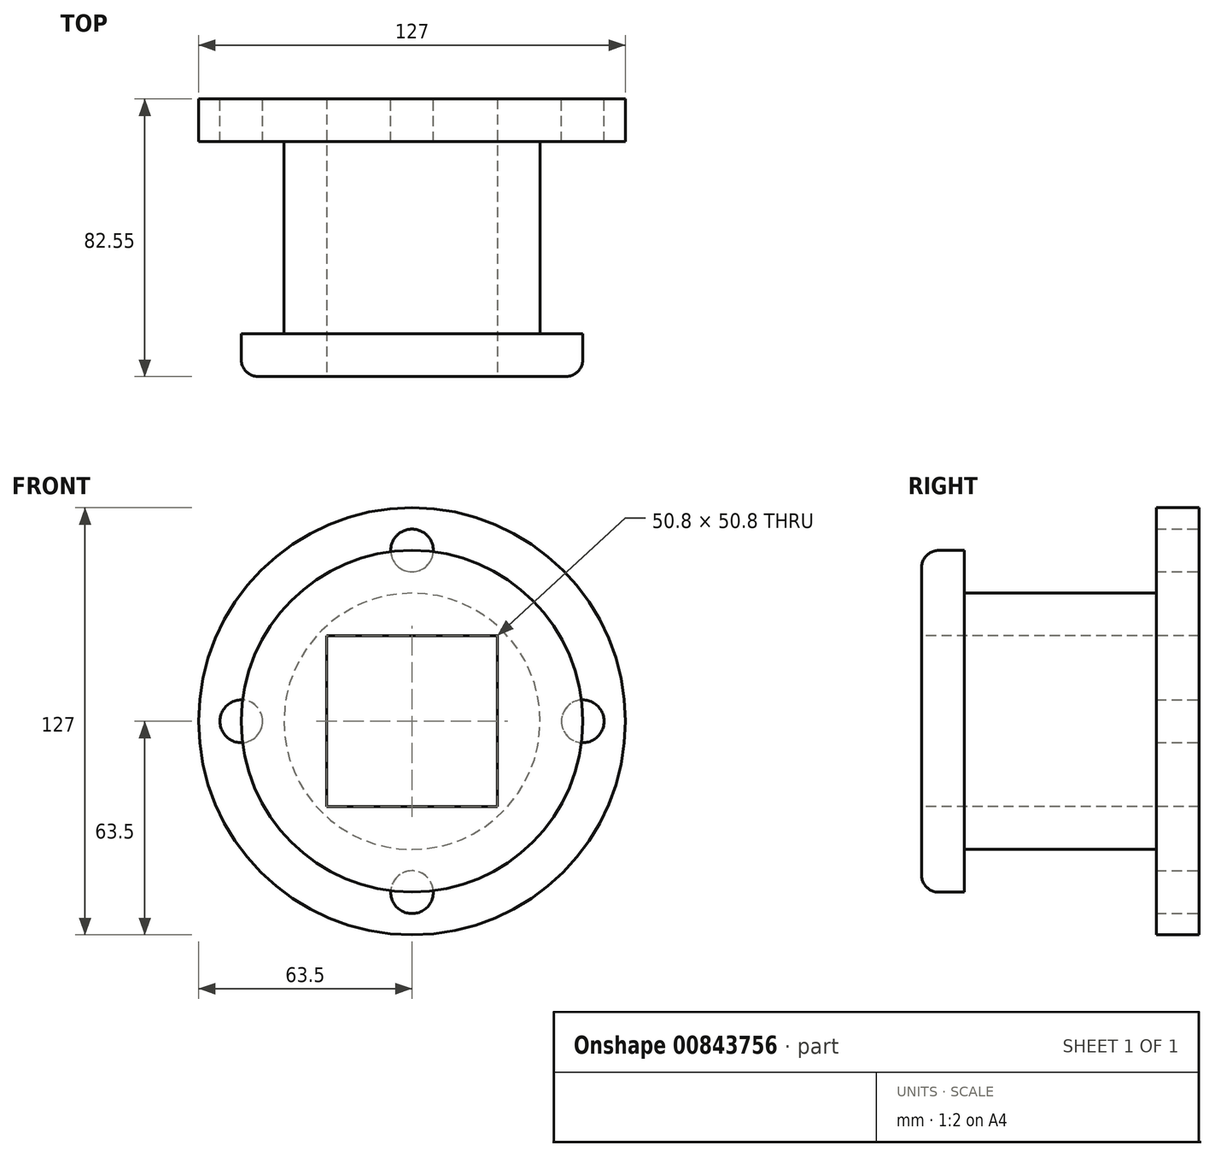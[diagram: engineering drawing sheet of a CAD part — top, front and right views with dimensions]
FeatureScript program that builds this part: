
annotation { "Feature Type Name" : "Feature", "Feature Type Description" : "" }
export const myFeature = defineFeature(function(context is Context, id is Id, definition is map)
    precondition{}
    {
        {
            var Q0;
            Q0=qCreatedBy(makeId("Front.planeOp"),FACE);
            var sketch = newSketch(context, id + "F0", { "sketchPlane" : qUnion([Q0])});
            skCircle(sketch, "E0", {"center": v(0, 0) * mm, "radius": 63.5 * mm});
            skSolve(sketch);
        }
        {
            var Q0;
            Q0 = qSketchRegion(id + "F0", true);
            extrude(context, id + "F1", {"entities" : qUnion([Q0]), "depth" : 12.7 * mm, "offsetDistance" : 25.4 * mm});
        }
        {
            var Q0;
            Q0=makeQuery(id+"F1.opExtrude","CAP_FACE",FACE,{"disambiguationData":[OSD([sQuery(id+"F0.wireOp",EDGE,"E0")])],"isStart":false});
            var sketch = newSketch(context, id + "F2", { "sketchPlane" : qUnion([Q0])});
            skCircle(sketch, "E1", {"center": v(0, 0) * mm, "radius": 38.1 * mm});
            skSolve(sketch);
        }
        {
            var Q0;
            Q0 = qSketchRegion(id + "F2", true);
            extrude(context, id + "F3", {"entities" : qUnion([Q0]), "operationType" : NewBodyOperationType.ADD, "depth" : 57.15 * mm, "offsetDistance" : 25.4 * mm});
        }
        {
            var Q0;
            Q0=makeQuery(id+"F3.opExtrude","CAP_FACE",FACE,{"disambiguationData":[OSD([sQuery(id+"F2.wireOp",EDGE,"E1")])],"isStart":false});
            var sketch = newSketch(context, id + "F4", { "sketchPlane" : qUnion([Q0])});
            skCircle(sketch, "E2", {"center": v(0, 0) * mm, "radius": 50.8 * mm});
            skSolve(sketch);
        }
        {
            var Q0;
            Q0 = qSketchRegion(id + "F4", true);
            extrude(context, id + "F5", {"entities" : qUnion([Q0]), "operationType" : NewBodyOperationType.ADD, "depth" : 12.7 * mm, "offsetDistance" : 25.4 * mm});
        }
        {
            var Q0;
            Q0=makeQuery(id+"F5.opExtrude","CAP_FACE",FACE,{"disambiguationData":[OSD([sQuery(id+"F4.wireOp",EDGE,"E2")])],"isStart":false});
            var sketch = newSketch(context, id + "F6", { "sketchPlane" : qUnion([Q0])});
            skLineSegment(sketch, "E3.bottom", {"start": v(-25.4, 25.4) * mm, "end": v(25.4, 25.4) * mm});
            skLineSegment(sketch, "E3.top", {"start": v(-25.4, -25.4) * mm, "end": v(25.4, -25.4) * mm});
            skLineSegment(sketch, "E3.left", {"start": v(-25.4, 25.4) * mm, "end": v(-25.4, -25.4) * mm});
            skLineSegment(sketch, "E3.right", {"start": v(25.4, 25.4) * mm, "end": v(25.4, -25.4) * mm});
            skPoint(sketch, "E3.middle", {"position": v(0, 0) * mm});
            skSolve(sketch);
        }
        {
            var Q0;
            Q0 = qSketchRegion(id + "F6", true);
            extrude(context, id + "F7", {"entities" : qUnion([Q0]), "operationType" : NewBodyOperationType.REMOVE, "oppositeDirection" : true, "depth" : 82.55 * mm, "offsetDistance" : 25.4 * mm});
        }
        {
            var Q0;
            Q0=makeQuery(id+"F1.opExtrude","CAP_FACE",FACE,{"disambiguationData":[OSD([sQuery(id+"F0.wireOp",EDGE,"E0")])],"isStart":true});
            var sketch = newSketch(context, id + "F8", { "sketchPlane" : qUnion([Q0])});
            skCircle(sketch, "E4", {"center": v(0, 50.8) * mm, "radius": 6.35 * mm});
            skCircle(sketch, "E5.1.0", {"center": v(-50.8, 0) * mm, "radius": 6.35 * mm});
            skCircle(sketch, "E5.2.0", {"center": v(0, -50.8) * mm, "radius": 6.35 * mm});
            skCircle(sketch, "E5.3.0", {"center": v(50.8, 0) * mm, "radius": 6.35 * mm});
            skPoint(sketch, "E5.center", {"position": v(0, 0) * mm});
            skSolve(sketch);
        }
        {
            var Q0;
            Q0=makeQuery(id+"F8.imprint","IMPRINT",FACE,{"disambiguationData":[TD([[makeQuery(id+"F8.imprint","IMPRINT",EDGE,{"derivedFrom":sQuery(id+"F8.wireOp",EDGE,"E4")}),1.0]])]});
            var Q1;
            Q1=makeQuery(id+"F8.imprint","IMPRINT",FACE,{"disambiguationData":[TD([[makeQuery(id+"F8.imprint","IMPRINT",EDGE,{"derivedFrom":sQuery(id+"F8.wireOp",EDGE,"E5.1.0")}),1.0]])]});
            var Q2;
            Q2=makeQuery(id+"F8.imprint","IMPRINT",FACE,{"disambiguationData":[TD([[makeQuery(id+"F8.imprint","IMPRINT",EDGE,{"derivedFrom":sQuery(id+"F8.wireOp",EDGE,"E5.2.0")}),1.0]])]});
            var Q3;
            Q3=makeQuery(id+"F8.imprint","IMPRINT",FACE,{"disambiguationData":[TD([[makeQuery(id+"F8.imprint","IMPRINT",EDGE,{"derivedFrom":sQuery(id+"F8.wireOp",EDGE,"E5.3.0")}),1.0]])]});
            extrude(context, id + "F9", {"entities" : qUnion([Q0, Q1, Q2, Q3]), "operationType" : NewBodyOperationType.REMOVE, "oppositeDirection" : true, "depth" : 12.7 * mm, "offsetDistance" : 25.4 * mm});
        }
        {
            var Q0;
            Q0=makeQuery(id+"F5.opExtrude","CAP_EDGE",EDGE,{"disambiguationData":[OSD([sQuery(id+"F4.wireOp",EDGE,"E2")])],"isStart":false});
            fillet(context, id + "F10", {"entities" : qUnion([Q0]), "radius" : 5.08 * mm, "tangentPropagation" : true, "allowEdgeOverflow" : false});
        }
    });
